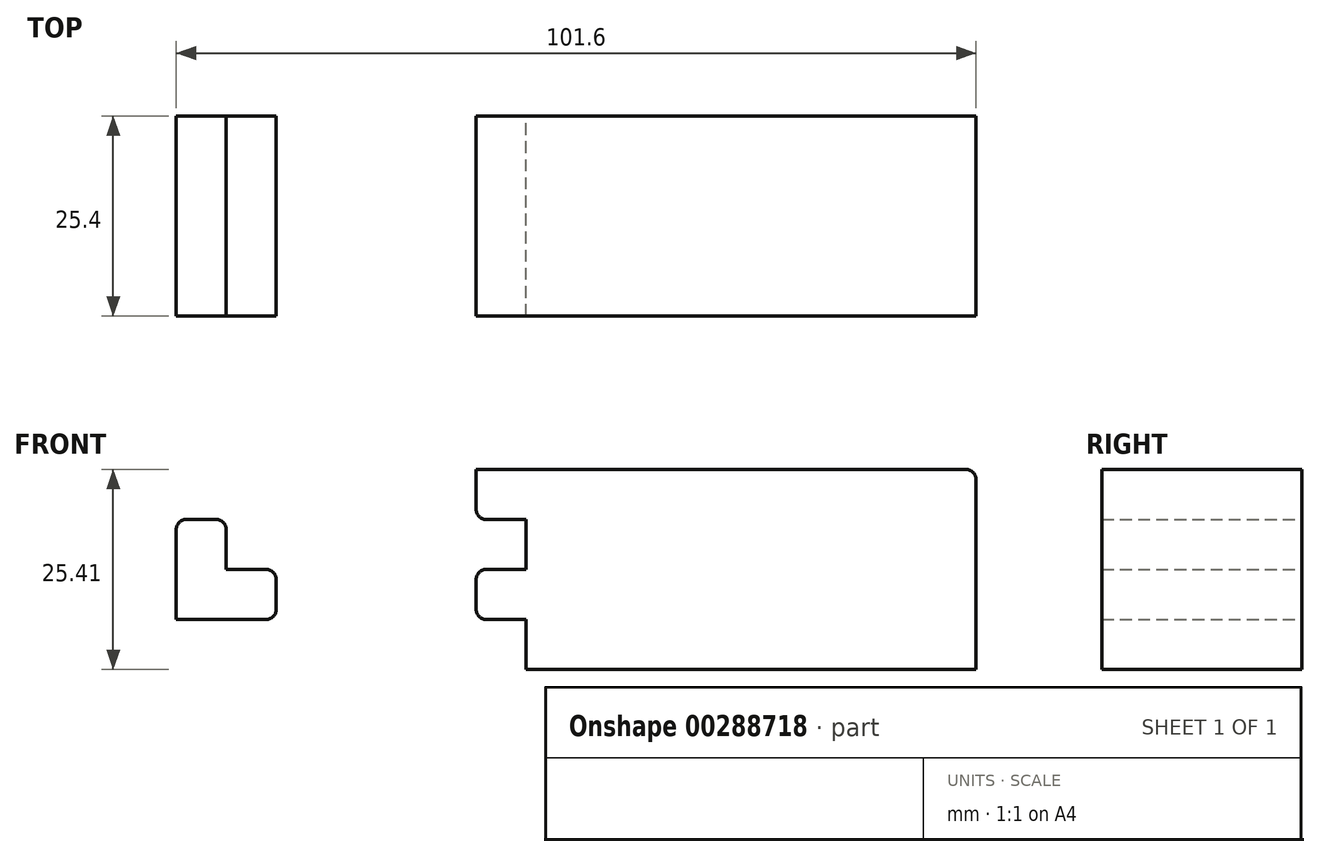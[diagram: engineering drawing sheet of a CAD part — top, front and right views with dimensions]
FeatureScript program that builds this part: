
annotation { "Feature Type Name" : "Feature", "Feature Type Description" : "" }
export const myFeature = defineFeature(function(context is Context, id is Id, definition is map)
    precondition{}
    {
        {
            var Q0;
            Q0=qCreatedBy(makeId("Front.planeOp"),FACE);
            var sketch = newSketch(context, id + "F0", { "sketchPlane" : qUnion([Q0])});
            skLineSegment(sketch, "E0.bottom", {"start": v(50.8, -15.87) * mm, "end": v(-50.8, -15.88) * mm});
            skLineSegment(sketch, "E0.top", {"start": v(50.8, 15.88) * mm, "end": v(-50.8, 15.88) * mm});
            skLineSegment(sketch, "E0.left", {"start": v(50.8, -15.87) * mm, "end": v(50.8, 15.88) * mm});
            skLineSegment(sketch, "E0.right", {"start": v(-50.8, -15.88) * mm, "end": v(-50.8, 15.88) * mm});
            skPoint(sketch, "E0.middle", {"position": v(0, 0) * mm});
            skLineSegment(sketch, "E1.bottom", {"start": v(-50.8, 15.88) * mm, "end": v(-38.1, 15.88) * mm});
            skLineSegment(sketch, "E1.top", {"start": v(-50.8, 9.53) * mm, "end": v(-38.1, 9.53) * mm});
            skLineSegment(sketch, "E1.left", {"start": v(-50.8, 15.88) * mm, "end": v(-50.8, 9.53) * mm});
            skLineSegment(sketch, "E1.right", {"start": v(-38.1, 15.88) * mm, "end": v(-38.1, 9.53) * mm});
            skLineSegment(sketch, "E2.bottom", {"start": v(-50.8, 9.53) * mm, "end": v(-44.45, 9.53) * mm});
            skLineSegment(sketch, "E2.top", {"start": v(-50.8, 3.18) * mm, "end": v(-44.45, 3.18) * mm});
            skLineSegment(sketch, "E2.left", {"start": v(-50.8, 9.53) * mm, "end": v(-50.8, 3.18) * mm});
            skLineSegment(sketch, "E2.right", {"start": v(-44.45, 9.53) * mm, "end": v(-44.45, 3.18) * mm});
            skLineSegment(sketch, "E3.bottom", {"start": v(-50.8, 3.18) * mm, "end": v(-38.1, 3.18) * mm});
            skLineSegment(sketch, "E3.top", {"start": v(-50.8, -3.17) * mm, "end": v(-38.1, -3.17) * mm});
            skLineSegment(sketch, "E3.left", {"start": v(-50.8, 3.18) * mm, "end": v(-50.8, -3.17) * mm});
            skLineSegment(sketch, "E3.right", {"start": v(-38.1, 3.18) * mm, "end": v(-38.1, -3.17) * mm});
            skLineSegment(sketch, "E4.bottom", {"start": v(-50.8, -3.17) * mm, "end": v(-44.45, -3.17) * mm});
            skLineSegment(sketch, "E4.top", {"start": v(-50.8, -9.52) * mm, "end": v(-44.45, -9.52) * mm});
            skLineSegment(sketch, "E4.left", {"start": v(-50.8, -3.17) * mm, "end": v(-50.8, -9.52) * mm});
            skLineSegment(sketch, "E4.right", {"start": v(-44.45, -3.17) * mm, "end": v(-44.45, -9.52) * mm});
            skLineSegment(sketch, "E5.bottom", {"start": v(-50.8, -9.52) * mm, "end": v(50.8, -9.52) * mm});
            skLineSegment(sketch, "E5.top", {"start": v(-50.8, -15.88) * mm, "end": v(50.8, -15.87) * mm});
            skLineSegment(sketch, "E5.left", {"start": v(-50.8, -9.52) * mm, "end": v(-50.8, -15.88) * mm});
            skLineSegment(sketch, "E5.right", {"start": v(50.8, -9.52) * mm, "end": v(50.8, -15.87) * mm});
            skLineSegment(sketch, "E6.MirrorCS", {"start": v(-12.7, 15.88) * mm, "end": v(-12.7, 9.53) * mm});
            skLineSegment(sketch, "E7.MirrorCS", {"start": v(0, 9.53) * mm, "end": v(-12.7, 9.53) * mm});
            skLineSegment(sketch, "E8.MirrorCS", {"start": v(0, 3.18) * mm, "end": v(-12.7, 3.18) * mm});
            skLineSegment(sketch, "E9.MirrorCS", {"start": v(-6.35, 9.53) * mm, "end": v(-6.35, 3.18) * mm});
            skLineSegment(sketch, "E10.MirrorCS", {"start": v(0, 9.53) * mm, "end": v(0, 3.18) * mm});
            skLineSegment(sketch, "E11.MirrorCS", {"start": v(-6.35, -3.17) * mm, "end": v(-6.35, -9.52) * mm});
            skLineSegment(sketch, "E12.MirrorCS", {"start": v(0, -3.17) * mm, "end": v(-6.35, -3.17) * mm});
            skLineSegment(sketch, "E13.MirrorCS", {"start": v(0, -3.17) * mm, "end": v(-12.7, -3.17) * mm});
            skLineSegment(sketch, "E14.MirrorCS", {"start": v(-12.7, 3.18) * mm, "end": v(-12.7, -3.17) * mm});
            skLineSegment(sketch, "E15.MirrorCS", {"start": v(0, 15.88) * mm, "end": v(0, 9.53) * mm});
            skLineSegment(sketch, "E16.MirrorCS", {"start": v(0, -15.87) * mm, "end": v(0, 15.88) * mm});
            skLineSegment(sketch, "E17.MirrorCS", {"start": v(12.7, 15.88) * mm, "end": v(12.7, 9.53) * mm});
            skLineSegment(sketch, "E18.MirrorCS", {"start": v(0, 9.53) * mm, "end": v(12.7, 9.53) * mm});
            skLineSegment(sketch, "E19.MirrorCS", {"start": v(6.35, 9.53) * mm, "end": v(6.35, 3.18) * mm});
            skLineSegment(sketch, "E20.MirrorCS", {"start": v(0, 3.18) * mm, "end": v(12.7, 3.18) * mm});
            skLineSegment(sketch, "E21.MirrorCS", {"start": v(12.7, 3.18) * mm, "end": v(12.7, -3.17) * mm});
            skLineSegment(sketch, "E22.MirrorCS", {"start": v(0, -3.17) * mm, "end": v(12.7, -3.17) * mm});
            skLineSegment(sketch, "E23.MirrorCS", {"start": v(6.35, -3.17) * mm, "end": v(6.35, -9.52) * mm});
            skLineSegment(sketch, "E24.MirrorCS", {"start": v(38.1, 15.88) * mm, "end": v(38.1, 9.53) * mm});
            skLineSegment(sketch, "E25.MirrorCS", {"start": v(50.8, 9.53) * mm, "end": v(38.1, 9.53) * mm});
            skLineSegment(sketch, "E26.MirrorCS", {"start": v(44.45, 9.53) * mm, "end": v(44.45, 3.18) * mm});
            skLineSegment(sketch, "E27.MirrorCS", {"start": v(50.8, 3.18) * mm, "end": v(38.1, 3.18) * mm});
            skLineSegment(sketch, "E28.MirrorCS", {"start": v(38.1, 3.18) * mm, "end": v(38.1, -3.17) * mm});
            skLineSegment(sketch, "E29.MirrorCS", {"start": v(50.8, -3.17) * mm, "end": v(38.1, -3.17) * mm});
            skLineSegment(sketch, "E30.MirrorCS", {"start": v(44.45, -3.17) * mm, "end": v(44.45, -9.52) * mm});
            skLineSegment(sketch, "E31", {"start": v(-6.35, -9.52) * mm, "end": v(6.35, -9.52) * mm});
            skSolve(sketch);
        }
        {
            var Q0;
            Q0=makeQuery(id+"F0.imprint","IMPRINT",FACE,{"disambiguationData":[TD([[makeQuery(id+"F0.imprint","IMPRINT",EDGE,{"derivedFrom":sQuery(id+"F0.wireOp",EDGE,"E1.bottom")}),-1.0]])]});
            var Q1;
            Q1=makeQuery(id+"F0.imprint","IMPRINT",FACE,{"disambiguationData":[TD([[makeQuery(id+"F0.imprint","IMPRINT",EDGE,{"derivedFrom":sQuery(id+"F0.wireOp",EDGE,"E2.bottom")}),-1.0]])]});
            var Q2;
            Q2=makeQuery(id+"F0.imprint","IMPRINT",FACE,{"disambiguationData":[TD([[makeQuery(id+"F0.imprint","IMPRINT",EDGE,{"derivedFrom":sQuery(id+"F0.wireOp",EDGE,"E3.top")}),1.0]])]});
            var Q3;
            Q3=makeQuery(id+"F0.imprint","IMPRINT",FACE,{"disambiguationData":[TD([[makeQuery(id+"F0.imprint","IMPRINT",EDGE,{"derivedFrom":sQuery(id+"F0.wireOp",EDGE,"E4.bottom")}),-1.0]])]});
            var Q4;
            {var subQ0=sQuery(id+"F0.wireOp",EDGE,"E5.left");Q4=makeQuery(id+"F0.imprint","IMPRINT",FACE,{"disambiguationData":[TD([[makeQuery(id+"F0.imprint","IMPRINT",EDGE,{"derivedFrom":subQ0}),1.0]])]});}
            var Q5;
            {var subQ0=sQuery(id+"F0.wireOp",EDGE,"E5.right");Q5=makeQuery(id+"F0.imprint","IMPRINT",FACE,{"disambiguationData":[TD([[makeQuery(id+"F0.imprint","IMPRINT",EDGE,{"derivedFrom":subQ0}),-1.0]])]});}
            var Q6;
            {var subQ5=sQuery(id+"F0.wireOp",EDGE,"E23.MirrorCS");Q6=makeQuery(id+"F0.imprint","IMPRINT",FACE,{"disambiguationData":[TD([[makeQuery(id+"F0.imprint","IMPRINT",EDGE,{"derivedFrom":subQ5}),-1.0]])]});}
            var Q7;
            {var subQ0=sQuery(id+"F0.wireOp",EDGE,"E11.MirrorCS");Q7=makeQuery(id+"F0.imprint","IMPRINT",FACE,{"disambiguationData":[TD([[makeQuery(id+"F0.imprint","IMPRINT",EDGE,{"derivedFrom":subQ0}),1.0]])]});}
            var Q8;
            {var subQ4=sQuery(id+"F0.wireOp",EDGE,"E14.MirrorCS");Q8=makeQuery(id+"F0.imprint","IMPRINT",FACE,{"disambiguationData":[TD([[makeQuery(id+"F0.imprint","IMPRINT",EDGE,{"derivedFrom":subQ4}),1.0]])]});}
            var Q9;
            {var subQ0=sQuery(id+"F0.wireOp",EDGE,"E21.MirrorCS");Q9=makeQuery(id+"F0.imprint","IMPRINT",FACE,{"disambiguationData":[TD([[makeQuery(id+"F0.imprint","IMPRINT",EDGE,{"derivedFrom":subQ0}),-1.0]])]});}
            var Q10;
            {var subQ5=sQuery(id+"F0.wireOp",EDGE,"E19.MirrorCS");Q10=makeQuery(id+"F0.imprint","IMPRINT",FACE,{"disambiguationData":[TD([[makeQuery(id+"F0.imprint","IMPRINT",EDGE,{"derivedFrom":subQ5}),-1.0]])]});}
            var Q11;
            {var subQ3=sQuery(id+"F0.wireOp",EDGE,"E9.MirrorCS");Q11=makeQuery(id+"F0.imprint","IMPRINT",FACE,{"disambiguationData":[TD([[makeQuery(id+"F0.imprint","IMPRINT",EDGE,{"derivedFrom":subQ3}),1.0]])]});}
            var Q12;
            {var subQ1=sQuery(id+"F0.wireOp",EDGE,"E6.MirrorCS");Q12=makeQuery(id+"F0.imprint","IMPRINT",FACE,{"disambiguationData":[TD([[makeQuery(id+"F0.imprint","IMPRINT",EDGE,{"derivedFrom":subQ1}),1.0]])]});}
            var Q13;
            {var subQ6=sQuery(id+"F0.wireOp",EDGE,"E17.MirrorCS");Q13=makeQuery(id+"F0.imprint","IMPRINT",FACE,{"disambiguationData":[TD([[makeQuery(id+"F0.imprint","IMPRINT",EDGE,{"derivedFrom":subQ6}),-1.0]])]});}
            var Q14;
            {var subQ0=sQuery(id+"F0.wireOp",EDGE,"E24.MirrorCS");Q14=makeQuery(id+"F0.imprint","IMPRINT",FACE,{"disambiguationData":[TD([[makeQuery(id+"F0.imprint","IMPRINT",EDGE,{"derivedFrom":subQ0}),1.0]])]});}
            var Q15;
            {var subQ5=sQuery(id+"F0.wireOp",EDGE,"E26.MirrorCS");Q15=makeQuery(id+"F0.imprint","IMPRINT",FACE,{"disambiguationData":[TD([[makeQuery(id+"F0.imprint","IMPRINT",EDGE,{"derivedFrom":subQ5}),1.0]])]});}
            var Q16;
            {var subQ0=sQuery(id+"F0.wireOp",EDGE,"E28.MirrorCS");Q16=makeQuery(id+"F0.imprint","IMPRINT",FACE,{"disambiguationData":[TD([[makeQuery(id+"F0.imprint","IMPRINT",EDGE,{"derivedFrom":subQ0}),1.0]])]});}
            var Q17;
            {var subQ5=sQuery(id+"F0.wireOp",EDGE,"E30.MirrorCS");Q17=makeQuery(id+"F0.imprint","IMPRINT",FACE,{"disambiguationData":[TD([[makeQuery(id+"F0.imprint","IMPRINT",EDGE,{"derivedFrom":subQ5}),1.0]])]});}
            var Q18;
            Q18=makeQuery(id+"F0.imprint","IMPRINT",FACE,{"disambiguationData":[TD([[makeQuery(id+"F0.imprint","IMPRINT",EDGE,{"derivedFrom":sQuery(id+"F0.wireOp",EDGE,"E1.top")}),-1.0]])]});
            var Q19;
            {var subQ6=sQuery(id+"F0.wireOp",EDGE,"E17.MirrorCS");Q19=makeQuery(id+"F0.imprint","IMPRINT",FACE,{"disambiguationData":[TD([[makeQuery(id+"F0.imprint","IMPRINT",EDGE,{"derivedFrom":subQ6}),1.0]])]});}
            extrude(context, id + "F1", {"entities" : qUnion([Q0, Q1, Q2, Q3, Q4, Q5, Q6, Q7, Q8, Q9, Q10, Q11, Q12, Q13, Q14, Q15, Q16, Q17, Q18, Q19]), "depth" : 25.4 * mm});
        }
        {
            var Q0;
            Q0=makeQuery(id+"F1.opExtrude","SWEPT_EDGE",EDGE,{"disambiguationData":[OSD([sQuery(id+"F0.wireOp",EDGE,"E1.top"),sQuery(id+"F0.wireOp",EDGE,"E1.right")])]});
            var Q1;
            Q1=makeQuery(id+"F1.opExtrude","SWEPT_EDGE",EDGE,{"disambiguationData":[OSD([sQuery(id+"F0.wireOp",EDGE,"E3.bottom"),sQuery(id+"F0.wireOp",EDGE,"E3.right")])]});
            var Q2;
            Q2=makeQuery(id+"F1.opExtrude","SWEPT_EDGE",EDGE,{"disambiguationData":[OSD([sQuery(id+"F0.wireOp",EDGE,"E3.top"),sQuery(id+"F0.wireOp",EDGE,"E3.right")])]});
            var Q3;
            Q3=makeQuery(id+"F1.opExtrude","SWEPT_EDGE",EDGE,{"disambiguationData":[OSD([sQuery(id+"F0.wireOp",EDGE,"E8.MirrorCS"),sQuery(id+"F0.wireOp",EDGE,"E14.MirrorCS")])]});
            var Q4;
            Q4=makeQuery(id+"F1.opExtrude","SWEPT_EDGE",EDGE,{"disambiguationData":[OSD([sQuery(id+"F0.wireOp",EDGE,"E6.MirrorCS"),sQuery(id+"F0.wireOp",EDGE,"E7.MirrorCS")])]});
            var Q5;
            Q5=makeQuery(id+"F1.opExtrude","SWEPT_EDGE",EDGE,{"disambiguationData":[OSD([sQuery(id+"F0.wireOp",EDGE,"E13.MirrorCS"),sQuery(id+"F0.wireOp",EDGE,"E14.MirrorCS")])]});
            var Q6;
            Q6=makeQuery(id+"F1.opExtrude","SWEPT_EDGE",EDGE,{"disambiguationData":[OSD([sQuery(id+"F0.wireOp",EDGE,"E1.bottom"),sQuery(id+"F0.wireOp",EDGE,"E1.left")])]});
            var Q7;
            Q7=makeQuery(id+"F1.opExtrude","SWEPT_EDGE",EDGE,{"disambiguationData":[OSD([sQuery(id+"F0.wireOp",EDGE,"E5.top"),sQuery(id+"F0.wireOp",EDGE,"E5.left")])]});
            var Q8;
            Q8=makeQuery(id+"F1.opExtrude","SWEPT_EDGE",EDGE,{"disambiguationData":[OSD([sQuery(id+"F0.wireOp",EDGE,"E17.MirrorCS"),sQuery(id+"F0.wireOp",EDGE,"E18.MirrorCS")])]});
            var Q9;
            Q9=makeQuery(id+"F1.opExtrude","SWEPT_EDGE",EDGE,{"disambiguationData":[OSD([sQuery(id+"F0.wireOp",EDGE,"E20.MirrorCS"),sQuery(id+"F0.wireOp",EDGE,"E21.MirrorCS")])]});
            var Q10;
            Q10=makeQuery(id+"F1.opExtrude","SWEPT_EDGE",EDGE,{"disambiguationData":[OSD([sQuery(id+"F0.wireOp",EDGE,"E21.MirrorCS"),sQuery(id+"F0.wireOp",EDGE,"E22.MirrorCS")])]});
            var Q11;
            Q11=makeQuery(id+"F1.opExtrude","SWEPT_EDGE",EDGE,{"disambiguationData":[OSD([sQuery(id+"F0.wireOp",EDGE,"E24.MirrorCS"),sQuery(id+"F0.wireOp",EDGE,"E25.MirrorCS")])]});
            var Q12;
            Q12=makeQuery(id+"F1.opExtrude","SWEPT_EDGE",EDGE,{"disambiguationData":[OSD([sQuery(id+"F0.wireOp",EDGE,"E27.MirrorCS"),sQuery(id+"F0.wireOp",EDGE,"E28.MirrorCS")])]});
            var Q13;
            Q13=makeQuery(id+"F1.opExtrude","SWEPT_EDGE",EDGE,{"disambiguationData":[OSD([sQuery(id+"F0.wireOp",EDGE,"E28.MirrorCS"),sQuery(id+"F0.wireOp",EDGE,"E29.MirrorCS")])]});
            var Q14;
            Q14=makeQuery(id+"F1.opExtrude","SWEPT_EDGE",EDGE,{"disambiguationData":[OSD([sQuery(id+"F0.wireOp",EDGE,"E0.top"),sQuery(id+"F0.wireOp",EDGE,"E0.left")])]});
            var Q15;
            Q15=makeQuery(id+"F1.opExtrude","SWEPT_EDGE",EDGE,{"disambiguationData":[OSD([sQuery(id+"F0.wireOp",EDGE,"E5.top"),sQuery(id+"F0.wireOp",EDGE,"E5.right")])]});
            fillet(context, id + "F2", {"entities" : qUnion([Q0, Q1, Q2, Q3, Q4, Q5, Q6, Q7, Q8, Q9, Q10, Q11, Q12, Q13, Q14, Q15]), "radius" : 1.27 * mm, "tangentPropagation" : true, "allowEdgeOverflow" : false});
        }
    });
